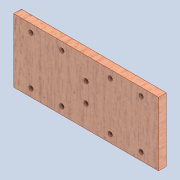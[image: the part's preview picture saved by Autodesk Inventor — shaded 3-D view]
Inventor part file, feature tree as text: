
AUTODESK INVENTOR PART (.ipt)
format: ipt  version: 2020 (Build 240168000, 168)  size: 164,352 bytes
history: native  units: mm
features: extrude x2, sketch x2
ambient origin geometry x8: Origin, YZ Plane, XZ Plane, XY Plane, X Axis, Y Axis, Z Axis, Center Point
bodies: Solid1 (feature_tree)
feature tree (4):
  extrude  "Extrusion1"  Depth=66.0mm
  extrude  "Extrusion4"  Depth=10.0mm
  sketch  "Sketch1"  dims[d0=150.0mm d1=66.0mm]
  sketch  "Sketch4"  dims[d2=8.0mm d3=0.0mm d19=4.5mm d20=18.0mm d21=8.0mm d22=8.0mm d23=32.0mm d24=18.0mm d26=32.0mm d27=0.0mm d28=0.0mm d29=10.0mm d30=10.0mm]
